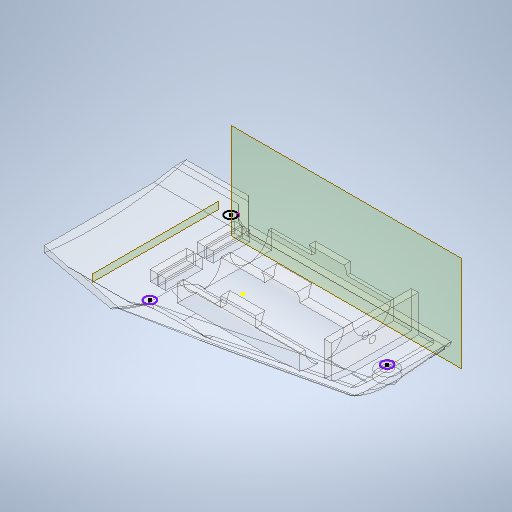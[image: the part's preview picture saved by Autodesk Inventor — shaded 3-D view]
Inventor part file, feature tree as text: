
AUTODESK INVENTOR PART (.ipt)
format: ipt  version: 2025 (Build 290162000, 162)  size: 3,508,736 bytes
history: native  units: in
note: dims shown in document units (in); Inventor stores cm internally (conversion verified against a paired STEP export)
features: extrude x44, sketch x37, fillet x33, other x28, reference x25, chamfer x10, projected_geometry x6, mirror x3, hole x1
ambient origin geometry x8: Origin, YZ Plane, XZ Plane, XY Plane, X Axis, Y Axis, Z Axis, Center Point
bodies: Body1 (feature_tree)
feature tree (187):
  other  "ソリッド1"
  sketch  "スケッチ1"
  extrude  "押し出し1"  Depth=3.3465in
  sketch  "スケッチ4"
  extrude  "押し出し4"  Depth=0.2756in
  extrude  "押し出し5"  Depth=9.8425in
  extrude  "押し出し6"  Depth=0.8661in TaperAngle=0.0deg
  extrude  "押し出し7"  Depth=0.8268in
  chamfer  "面取り1"  Distance=0.1181in
  chamfer  "面取り2"  Distance=0.1181in
  chamfer  "面取り3"  Distance=1.8504in
  chamfer  "面取り4"  Distance=1.1024in
  other  "作業平面3"
  other  "作業平面5"
  extrude  "押し出し8"  Depth=1.5354in
  other  "作業平面6"
  mirror  "ミラー1"
  chamfer  "面取り5"  Distance=3.3465in
  extrude  "押し出し9"  Depth=3.3465in TaperAngle=0.0deg
  fillet  "フィレット27"  Radius=3.3465in
  fillet  "フィレット28"  Radius=3.3465in
  fillet  "フィレット29"  Radius=0.1181in
  fillet  "フィレット30"  Radius=0.1181in
  fillet  "フィレット32"  Radius=0.1181in
  fillet  "フィレット35"  Radius=0.1181in
  fillet  "フィレット36"  Radius=0.3937in
  fillet  "フィレット37"  Radius=0.1575in
  fillet  "フィレット38"  Radius=0.7087in
  fillet  "フィレット42"  [1 undecoded]
  fillet  "フィレット43"  Radius=0.3543in
  fillet  "フィレット44"  Radius=1.9685in
  fillet  "フィレット45"  Radius=2.0866in
  other  "作業平面7"
  extrude  "押し出し10"  Depth=0.1969in
  fillet  "フィレット46"  Radius=0.1969in
  other  "作業平面8"
  extrude  "押し出し11"  Depth=0.7874in
  sketch  "スケッチ10"
  extrude  "押し出し12"  Depth=0.0787in
  extrude  "押し出し13"  Depth=0.3937in
  chamfer  "面取り6"  Distance=0.1181in
  sketch  "スケッチ11"
  chamfer  "面取り7"  Distance=0.1181in
  extrude  "押し出し14"  Depth=0.0354in
  chamfer  "面取り8"  Distance=0.0394in
  chamfer  "面取り9"  Distance=0.0787in
  extrude  "押し出し15"  Depth=0.0118in
  chamfer  "面取り10"  Distance=0.0354in
  other  "作業平面9"
  other  "作業平面10"
  extrude  "押し出し16"  [1 undecoded]
  fillet  "フィレット47"  Radius=0.0394in
  fillet  "フィレット48"  Radius=0.0394in
  fillet  "フィレット49"  Radius=0.0394in
  mirror  "ミラー7"
  mirror  "ミラー8"
  fillet  "フィレット58"  Radius=0.8268in
  fillet  "フィレット59"  Radius=0.0787in
  fillet  "フィレット60"  Radius=0.8268in
  fillet  "フィレット61"  Radius=1.1681in
  fillet  "フィレット62"  Radius=1.1681in
  fillet  "フィレット63"  Radius=0.6299in
  other  "作業平面11"
  extrude  "押し出し17"  TaperAngle=45.0deg  [1 undecoded]
  extrude  "押し出し18"  Depth=0.3937in
  extrude  "押し出し19"  Depth=1.1811in TaperAngle=0.0deg
  extrude  "押し出し20"  Depth=0.3543in TaperAngle=45.0deg
  other  "作業平面13"
  extrude  "押し出し21"  Depth=0.0787in
  fillet  "フィレット66"  Radius=0.1181in
  fillet  "フィレット67"  Radius=0.0709in
  extrude  "押し出し22"  Depth=0.0394in TaperAngle=45.0deg
  other  "作業平面14"
  extrude  "押し出し23"  Depth=0.0394in TaperAngle=45.0deg
  other  "作業平面15"
  extrude  "押し出し24"  Depth=0.0591in TaperAngle=0.0deg
  extrude  "押し出し25"  Depth=0.1969in TaperAngle=45.0deg
  other  "作業平面16"
  extrude  "押し出し26"  Depth=0.0591in TaperAngle=0.0deg
  extrude  "押し出し27"  Depth=3.937in
  other  "作業平面17"
  extrude  "押し出し28"  Depth=1.9685in
  extrude  "押し出し29"  Depth=0.1181in
  sketch  "スケッチ29"
  extrude  "押し出し30"  Depth=0.1181in
  extrude  "押し出し31"  Depth=0.0787in
  extrude  "押し出し32"  Depth=0.0197in
  extrude  "押し出し33"  Depth=0.0197in
  other  "作業平面18"
  extrude  "押し出し34"  Depth=0.3937in
  extrude  "押し出し35"  Depth=0.1181in
  fillet  "フィレット68"  [1 undecoded]
  fillet  "フィレット69"  Radius=1.1811in
  fillet  "フィレット70"  Radius=0.0787in
  fillet  "フィレット71"  Radius=0.1181in
  fillet  "フィレット72"  Radius=0.0197in
  extrude  "押し出し36"  Depth=0.0787in TaperAngle=0.0deg
  other  "作業平面19"
  fillet  "フィレット74"  Radius=0.9949in
  fillet  "フィレット75"  Radius=0.3937in
  fillet  "フィレット76"  Radius=0.0472in
  sketch  "スケッチ33"
  extrude  "押し出し39"  Depth=0.0669in
  extrude  "押し出し40"  Depth=0.0079in
  sketch  "スケッチ35"
  extrude  "押し出し41"  Depth=0.2756in
  other  "作業平面20"
  extrude  "押し出し42"  Depth=0.3543in
  sketch  "スケッチ37"
  extrude  "押し出し43"  Depth=0.3543in
  extrude  "押し出し44"  Depth=0.2756in
  sketch  "スケッチ38"
  hole  "穴2"  [1 undecoded]
  other  "作業平面21"
  sketch  "スケッチ40"
  extrude  "押し出し49"  Depth=0.0787in
  extrude  "押し出し50"  Depth=0.0079in
  extrude  "押し出し51"  Depth=0.1181in
  other  "作業平面22"
  extrude  "押し出し57"  Depth=0.0787in
  projected_geometry  "投影ループ2"
  sketch  "スケッチ5"
  projected_geometry  "投影ループ3"
  sketch  "スケッチ6"
  projected_geometry  "投影ループ4"
  other  "作業平面2"
  other  "作業平面4"
  sketch  "スケッチ7"
  sketch  "スケッチ8"
  projected_geometry  "投影ループ5"
  sketch  "スケッチ9"
  sketch  "スケッチ12"
  sketch  "スケッチ13"
  sketch  "スケッチ14"
  sketch  "スケッチ15"
  sketch  "スケッチ16"
  sketch  "スケッチ18"
  sketch  "スケッチ19"
  sketch  "スケッチ20"
  sketch  "スケッチ21"
  reference  "参照1"
  reference  "参照2"
  reference  "参照3"
  reference  "参照4"
  reference  "参照5"
  sketch  "スケッチ22"
  reference  "参照6"
  reference  "参照7"
  sketch  "スケッチ23"
  reference  "参照8"
  reference  "参照9"
  reference  "参照10"
  reference  "参照11"
  reference  "参照12"
  reference  "参照13"
  sketch  "スケッチ24"
  projected_geometry  "投影ループ6"
  sketch  "スケッチ25"
  sketch  "スケッチ26"
  sketch  "スケッチ27"
  sketch  "スケッチ28"
  reference  "参照14"
  reference  "参照15"
  other  "スケッチ円形状パターン1"
  sketch  "スケッチ30"
  reference  "参照16"
  sketch  "スケッチ31"
  reference  "参照17"
  reference  "参照18"
  reference  "参照19"
  reference  "参照21"
  reference  "参照22"
  reference  "参照23"
  reference  "参照24"
  reference  "参照25"
  reference  "参照29"
  sketch  "スケッチ32"
  sketch  "スケッチ34"
  sketch  "スケッチ36"
  projected_geometry  "投影ループ7"
  sketch  "スケッチ44"
  other  "<userpath>\OneDrive\ドキュメント\New Controller\Hardware\Assembly.iam"
  other  "Assembly.iam"
  other  "Nano33BLE:1"
  other  "Cuicuit:1"
  other  "switch:1"
  other  "mini vibrator:1"
note: 5 required parameter values undecoded (feature->parameter linkage not recoverable at this tier; creation-order binding heuristic only, values carry confidence <= 0.55)
